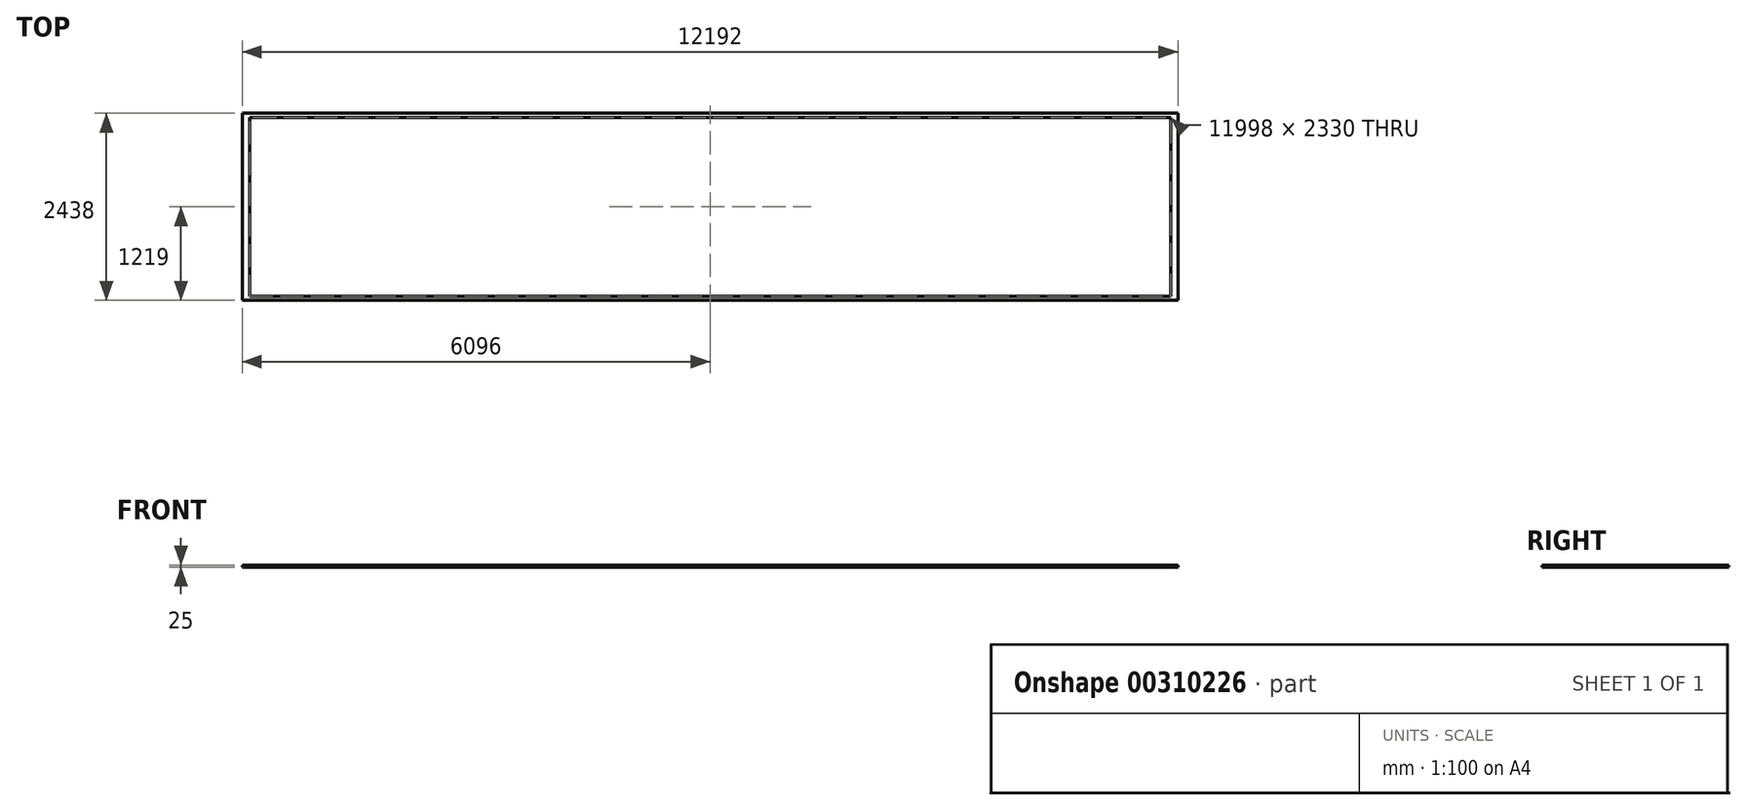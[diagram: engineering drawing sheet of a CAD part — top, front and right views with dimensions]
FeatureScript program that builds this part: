
annotation { "Feature Type Name" : "Feature", "Feature Type Description" : "" }
export const myFeature = defineFeature(function(context is Context, id is Id, definition is map)
    precondition{}
    {
        {
            var Q0;
            Q0=qCreatedBy(makeId("Top.planeOp"),FACE);
            var sketch = newSketch(context, id + "F0", { "sketchPlane" : qUnion([Q0])});
            skLineSegment(sketch, "E0.bottom", {"start": v(5999, 1165) * mm, "end": v(-5999, 1165) * mm});
            skLineSegment(sketch, "E0.top", {"start": v(5999, -1165) * mm, "end": v(-5999, -1165) * mm});
            skLineSegment(sketch, "E0.left", {"start": v(5999, 1165) * mm, "end": v(5999, -1165) * mm});
            skLineSegment(sketch, "E0.right", {"start": v(-5999, 1165) * mm, "end": v(-5999, -1165) * mm});
            skPoint(sketch, "E0.middle", {"position": v(0, 0) * mm});
            skLineSegment(sketch, "E1.bottom", {"start": v(6096, -1219) * mm, "end": v(-6096, -1219) * mm});
            skLineSegment(sketch, "E1.top", {"start": v(6096, 1219) * mm, "end": v(-6096, 1219) * mm});
            skLineSegment(sketch, "E1.left", {"start": v(6096, -1219) * mm, "end": v(6096, 1219) * mm});
            skLineSegment(sketch, "E1.right", {"start": v(-6096, -1219) * mm, "end": v(-6096, 1219) * mm});
            skLineSegment(sketch, "E2.bottom", {"start": v(-5583.56, -1143) * mm, "end": v(-6608.44, -1143) * mm});
            skLineSegment(sketch, "E2.top", {"start": v(-5583.56, 1143) * mm, "end": v(-6608.44, 1143) * mm});
            skLineSegment(sketch, "E2.left", {"start": v(-6608.44, -1143) * mm, "end": v(-6608.44, 1143) * mm});
            skLineSegment(sketch, "E2.right", {"start": v(-5583.56, -1143) * mm, "end": v(-5583.56, 1143) * mm});
            skPoint(sketch, "E2.middle", {"position": v(-6096, 0) * mm});
            skPoint(sketch, "E2.middle.positionSnap0", {"position": v(-6096, 0) * mm});
            skPoint(sketch, "E2.centerSnap0", {"position": v(-6096, 0) * mm});
            skSolve(sketch);
        }
        {
            var Q0;
            {var subQ0=sQuery(id+"F0.wireOp",EDGE,"E2.top");var subQ1=sQuery(id+"F0.wireOp",EDGE,"E0.right");var subQ2=makeQuery(id+"F0.imprint","INTERSECT",VERTEX,{"derivedFrom":[subQ1,subQ0]});Q0=makeQuery(id+"F0.imprint","IMPRINT",FACE,{"disambiguationData":[TD([[makeQuery(id+"F0.imprint","IMPRINT",EDGE,{"disambiguationData":[TD([[subQ2,-1.0]])],"derivedFrom":subQ1}),-1.0]])]});}
            var Q1;
            {var subQ10=sQuery(id+"F0.wireOp",EDGE,"E0.bottom");Q1=makeQuery(id+"F0.imprint","IMPRINT",FACE,{"disambiguationData":[TD([[makeQuery(id+"F0.imprint","IMPRINT",EDGE,{"derivedFrom":subQ10}),-1.0]])]});}
            extrude(context, id + "F1", {"entities" : qUnion([Q0, Q1]), "depth" : 25 * mm});
        }
    });
